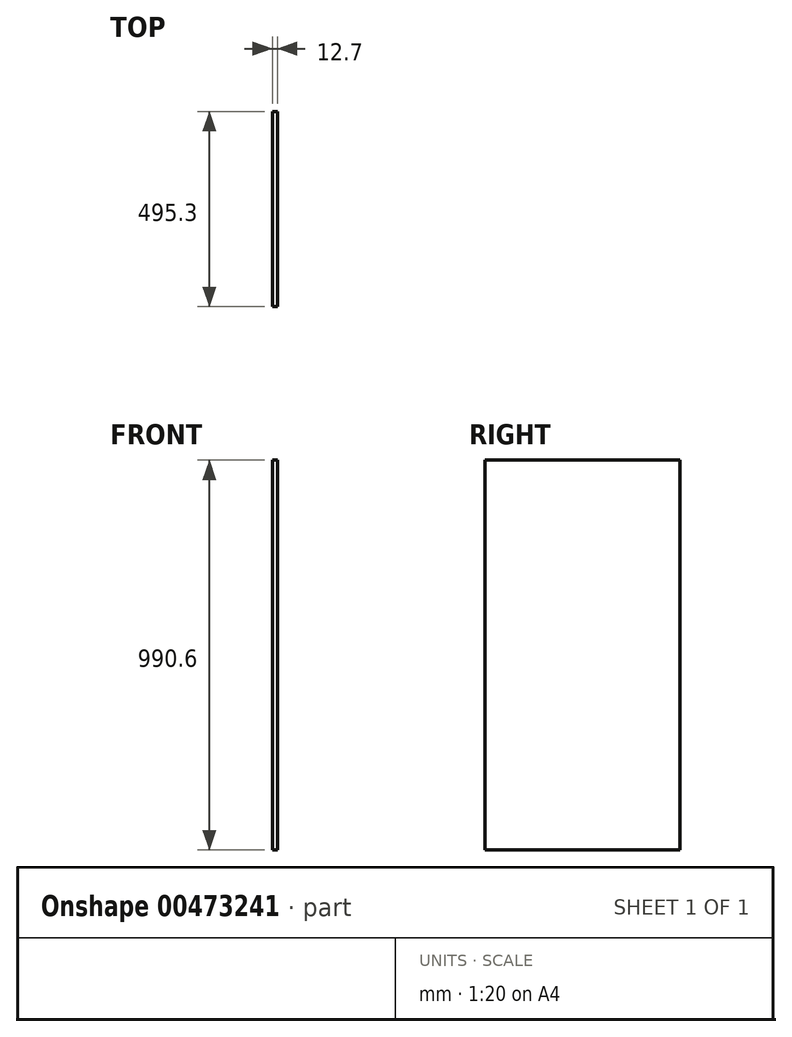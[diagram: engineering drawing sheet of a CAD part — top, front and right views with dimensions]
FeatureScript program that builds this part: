
annotation { "Feature Type Name" : "Feature", "Feature Type Description" : "" }
export const myFeature = defineFeature(function(context is Context, id is Id, definition is map)
    precondition{}
    {
        {
            var Q0;
            Q0=qCreatedBy(makeId("Right.planeOp"),FACE);
            var sketch = newSketch(context, id + "F0", { "sketchPlane" : qUnion([Q0])});
            skLineSegment(sketch, "E0.bottom", {"start": v(247.65, 495.3) * mm, "end": v(-247.65, 495.3) * mm});
            skLineSegment(sketch, "E0.top", {"start": v(247.65, -495.3) * mm, "end": v(-247.65, -495.3) * mm});
            skLineSegment(sketch, "E0.left", {"start": v(247.65, 495.3) * mm, "end": v(247.65, -495.3) * mm});
            skLineSegment(sketch, "E0.right", {"start": v(-247.65, 495.3) * mm, "end": v(-247.65, -495.3) * mm});
            skPoint(sketch, "E0.middle", {"position": v(0, 0) * mm});
            skSolve(sketch);
        }
        {
            var Q0;
            Q0=makeQuery(id+"F0.imprint","IMPRINT",FACE,{"disambiguationData":[TD([[makeQuery(id+"F0.imprint","IMPRINT",EDGE,{"derivedFrom":sQuery(id+"F0.wireOp",EDGE,"E0.bottom")}),1.0]])]});
            extrude(context, id + "F1", {"entities" : qUnion([Q0]), "depth" : 12.7 * mm});
        }
    });
